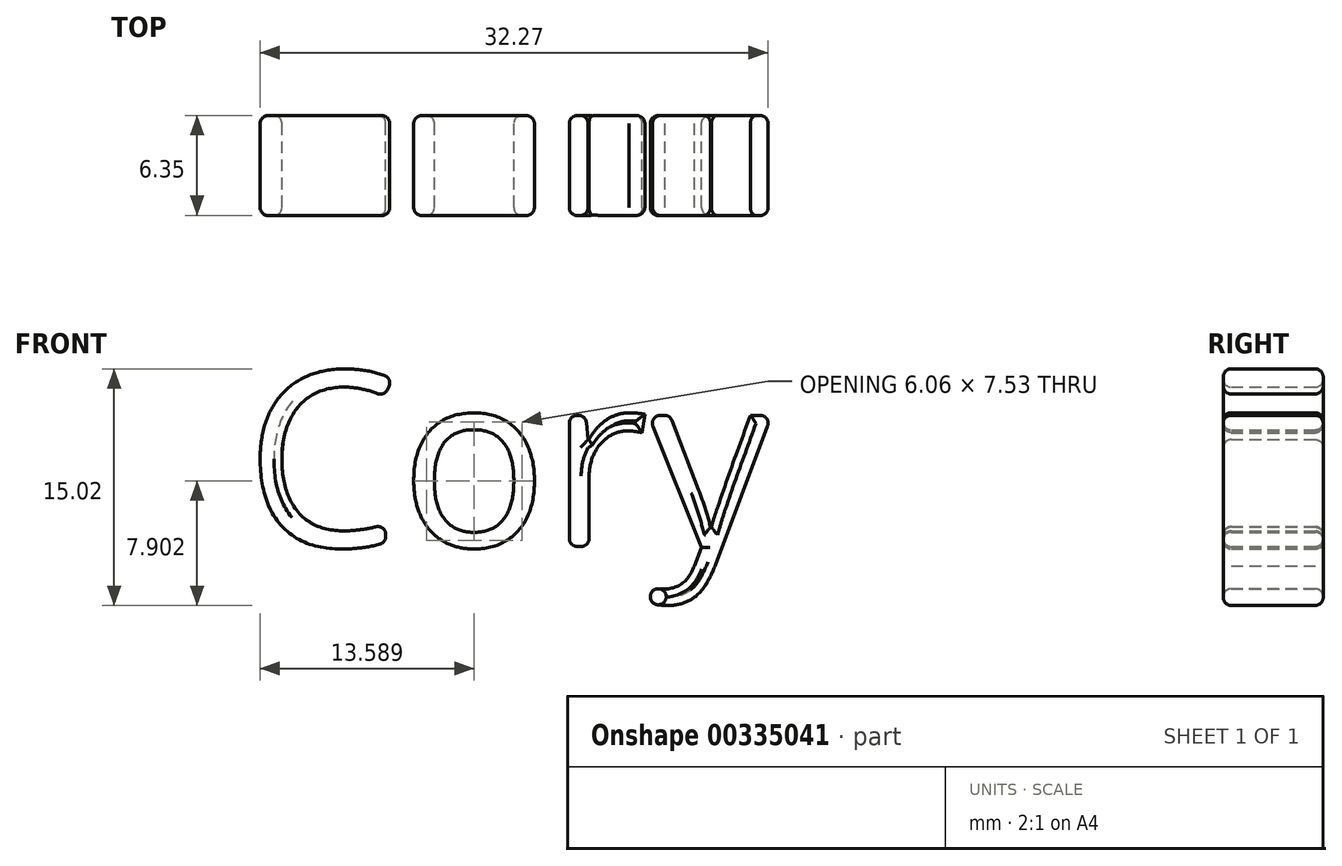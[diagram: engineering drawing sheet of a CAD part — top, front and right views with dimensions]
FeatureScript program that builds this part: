
annotation { "Feature Type Name" : "Feature", "Feature Type Description" : "" }
export const myFeature = defineFeature(function(context is Context, id is Id, definition is map)
    precondition{}
    {
        {
            var Q0;
            Q0=qCreatedBy(makeId("Front.planeOp"),FACE);
            var sketch = newSketch(context, id + "F0", { "sketchPlane" : qUnion([Q0])});
            skText(sketch, "E0", { "text": "Cory\n", "fontName": "OpenSans-Regular.ttf"});
            const initialGuessF0  = {"E0": [-0.05929, 0.0377, 1, 0, 0.01122]};
            skSetInitialGuess(sketch, initialGuessF0);
            skSolve(sketch);
        }
        {
            var Q0;
            Q0 = qSketchRegion(id + "F0", true);
            extrude(context, id + "F1", {"entities" : qUnion([Q0]), "depth" : 6.35 * mm});
        }
        {
            var Q0;
            Q0=makeQuery(id+"F1.opExtrude","SWEPT_FACE",FACE,{"disambiguationData":[OSD([sQuery(id+"F0.wireOp",EDGE,"E0.sketch_text.stroke-9")])]});
            var Q1;
            Q1=makeQuery(id+"F1.opExtrude","SWEPT_FACE",FACE,{"disambiguationData":[OSD([sQuery(id+"F0.wireOp",EDGE,"E0.sketch_text.stroke-8")])]});
            var Q2;
            Q2=makeQuery(id+"F1.opExtrude","CAP_EDGE",EDGE,{"disambiguationData":[OSD([sQuery(id+"F0.wireOp",EDGE,"E0.sketch_text.stroke-12")])],"isStart":false});
            var Q3;
            Q3=makeQuery(id+"F1.opExtrude","CAP_FACE",FACE,{"disambiguationData":[OSD([sQuery(id+"F0.wireOp",EDGE,"E0.sketch_text.stroke-0"),sQuery(id+"F0.wireOp",EDGE,"E0.sketch_text.stroke-1"),sQuery(id+"F0.wireOp",EDGE,"E0.sketch_text.stroke-2"),sQuery(id+"F0.wireOp",EDGE,"E0.sketch_text.stroke-3"),sQuery(id+"F0.wireOp",EDGE,"E0.sketch_text.stroke-4"),sQuery(id+"F0.wireOp",EDGE,"E0.sketch_text.stroke-5"),sQuery(id+"F0.wireOp",EDGE,"E0.sketch_text.stroke-6"),sQuery(id+"F0.wireOp",EDGE,"E0.sketch_text.stroke-7"),sQuery(id+"F0.wireOp",EDGE,"E0.sketch_text.stroke-8"),sQuery(id+"F0.wireOp",EDGE,"E0.sketch_text.stroke-9"),sQuery(id+"F0.wireOp",EDGE,"E0.sketch_text.stroke-10"),sQuery(id+"F0.wireOp",EDGE,"E0.sketch_text.stroke-11"),sQuery(id+"F0.wireOp",EDGE,"E0.sketch_text.stroke-12"),sQuery(id+"F0.wireOp",EDGE,"E0.sketch_text.stroke-13"),sQuery(id+"F0.wireOp",EDGE,"E0.sketch_text.stroke-14")])],"isStart":false});
            var Q4;
            Q4=makeQuery(id+"F1.opExtrude","SWEPT_FACE",FACE,{"disambiguationData":[OSD([sQuery(id+"F0.wireOp",EDGE,"E0.sketch_text.stroke-10")])]});
            var Q5;
            Q5=makeQuery(id+"F1.opExtrude","SWEPT_FACE",FACE,{"disambiguationData":[OSD([sQuery(id+"F0.wireOp",EDGE,"E0.sketch_text.stroke-11")])]});
            var Q6;
            Q6=makeQuery(id+"F1.opExtrude","SWEPT_FACE",FACE,{"disambiguationData":[OSD([sQuery(id+"F0.wireOp",EDGE,"E0.sketch_text.stroke-12")])]});
            var Q7;
            Q7=makeQuery(id+"F1.opExtrude","SWEPT_EDGE",EDGE,{"disambiguationData":[OSD([sQuery(id+"F0.wireOp",EDGE,"E0.sketch_text.stroke-4"),sQuery(id+"F0.wireOp",EDGE,"E0.sketch_text.stroke-5")])]});
            var Q8;
            Q8=makeQuery(id+"F1.opExtrude","SWEPT_FACE",FACE,{"disambiguationData":[OSD([sQuery(id+"F0.wireOp",EDGE,"E0.sketch_text.stroke-3")])]});
            var Q9;
            Q9=makeQuery(id+"F1.opExtrude","SWEPT_FACE",FACE,{"disambiguationData":[OSD([sQuery(id+"F0.wireOp",EDGE,"E0.sketch_text.stroke-2")])]});
            var Q10;
            Q10=makeQuery(id+"F1.opExtrude","SWEPT_FACE",FACE,{"disambiguationData":[OSD([sQuery(id+"F0.wireOp",EDGE,"E0.sketch_text.stroke-1")])]});
            var Q11;
            Q11=makeQuery(id+"F1.opExtrude","SWEPT_EDGE",EDGE,{"disambiguationData":[OSD([sQuery(id+"F0.wireOp",EDGE,"E0.sketch_text.stroke-5"),sQuery(id+"F0.wireOp",EDGE,"E0.sketch_text.stroke-6")])]});
            var Q12;
            Q12=makeQuery(id+"F1.opExtrude","SWEPT_FACE",FACE,{"disambiguationData":[OSD([sQuery(id+"F0.wireOp",EDGE,"E0.sketch_text.stroke-5")])]});
            var Q13;
            Q13=makeQuery(id+"F1.opExtrude","CAP_FACE",FACE,{"disambiguationData":[OSD([sQuery(id+"F0.wireOp",EDGE,"E0.sketch_text.stroke-15"),sQuery(id+"F0.wireOp",EDGE,"E0.sketch_text.stroke-16"),sQuery(id+"F0.wireOp",EDGE,"E0.sketch_text.stroke-17"),sQuery(id+"F0.wireOp",EDGE,"E0.sketch_text.stroke-18"),sQuery(id+"F0.wireOp",EDGE,"E0.sketch_text.stroke-19"),sQuery(id+"F0.wireOp",EDGE,"E0.sketch_text.stroke-20"),sQuery(id+"F0.wireOp",EDGE,"E0.sketch_text.stroke-21"),sQuery(id+"F0.wireOp",EDGE,"E0.sketch_text.stroke-22"),sQuery(id+"F0.wireOp",EDGE,"E0.sketch_text.stroke-23"),sQuery(id+"F0.wireOp",EDGE,"E0.sketch_text.stroke-24"),sQuery(id+"F0.wireOp",EDGE,"E0.sketch_text.stroke-25"),sQuery(id+"F0.wireOp",EDGE,"E0.sketch_text.stroke-26"),sQuery(id+"F0.wireOp",EDGE,"E0.sketch_text.stroke-27"),sQuery(id+"F0.wireOp",EDGE,"E0.sketch_text.stroke-28"),sQuery(id+"F0.wireOp",EDGE,"E0.sketch_text.stroke-29"),sQuery(id+"F0.wireOp",EDGE,"E0.sketch_text.stroke-30"),sQuery(id+"F0.wireOp",EDGE,"E0.sketch_text.stroke-31")])],"isStart":false});
            var Q14;
            Q14=makeQuery(id+"F1.opExtrude","CAP_FACE",FACE,{"disambiguationData":[OSD([sQuery(id+"F0.wireOp",EDGE,"E0.sketch_text.stroke-15"),sQuery(id+"F0.wireOp",EDGE,"E0.sketch_text.stroke-16"),sQuery(id+"F0.wireOp",EDGE,"E0.sketch_text.stroke-17"),sQuery(id+"F0.wireOp",EDGE,"E0.sketch_text.stroke-18"),sQuery(id+"F0.wireOp",EDGE,"E0.sketch_text.stroke-19"),sQuery(id+"F0.wireOp",EDGE,"E0.sketch_text.stroke-20"),sQuery(id+"F0.wireOp",EDGE,"E0.sketch_text.stroke-21"),sQuery(id+"F0.wireOp",EDGE,"E0.sketch_text.stroke-22"),sQuery(id+"F0.wireOp",EDGE,"E0.sketch_text.stroke-23"),sQuery(id+"F0.wireOp",EDGE,"E0.sketch_text.stroke-24"),sQuery(id+"F0.wireOp",EDGE,"E0.sketch_text.stroke-25"),sQuery(id+"F0.wireOp",EDGE,"E0.sketch_text.stroke-26"),sQuery(id+"F0.wireOp",EDGE,"E0.sketch_text.stroke-27"),sQuery(id+"F0.wireOp",EDGE,"E0.sketch_text.stroke-28"),sQuery(id+"F0.wireOp",EDGE,"E0.sketch_text.stroke-29"),sQuery(id+"F0.wireOp",EDGE,"E0.sketch_text.stroke-30"),sQuery(id+"F0.wireOp",EDGE,"E0.sketch_text.stroke-31")])],"isStart":true});
            var Q15;
            Q15=makeQuery(id+"F1.opExtrude","CAP_FACE",FACE,{"disambiguationData":[OSD([sQuery(id+"F0.wireOp",EDGE,"E0.sketch_text.stroke-32"),sQuery(id+"F0.wireOp",EDGE,"E0.sketch_text.stroke-33"),sQuery(id+"F0.wireOp",EDGE,"E0.sketch_text.stroke-34"),sQuery(id+"F0.wireOp",EDGE,"E0.sketch_text.stroke-35"),sQuery(id+"F0.wireOp",EDGE,"E0.sketch_text.stroke-36"),sQuery(id+"F0.wireOp",EDGE,"E0.sketch_text.stroke-37"),sQuery(id+"F0.wireOp",EDGE,"E0.sketch_text.stroke-38"),sQuery(id+"F0.wireOp",EDGE,"E0.sketch_text.stroke-39"),sQuery(id+"F0.wireOp",EDGE,"E0.sketch_text.stroke-40"),sQuery(id+"F0.wireOp",EDGE,"E0.sketch_text.stroke-41"),sQuery(id+"F0.wireOp",EDGE,"E0.sketch_text.stroke-42"),sQuery(id+"F0.wireOp",EDGE,"E0.sketch_text.stroke-43"),sQuery(id+"F0.wireOp",EDGE,"E0.sketch_text.stroke-44")])],"isStart":true});
            var Q16;
            Q16=makeQuery(id+"F1.opExtrude","SWEPT_FACE",FACE,{"disambiguationData":[OSD([sQuery(id+"F0.wireOp",EDGE,"E0.sketch_text.stroke-37")])]});
            var Q17;
            Q17=makeQuery(id+"F1.opExtrude","SWEPT_EDGE",EDGE,{"disambiguationData":[OSD([sQuery(id+"F0.wireOp",EDGE,"E0.sketch_text.stroke-38"),sQuery(id+"F0.wireOp",EDGE,"E0.sketch_text.stroke-39")])]});
            var Q18;
            Q18=makeQuery(id+"F1.opExtrude","SWEPT_FACE",FACE,{"disambiguationData":[OSD([sQuery(id+"F0.wireOp",EDGE,"E0.sketch_text.stroke-15")])]});
            var Q19;
            Q19=makeQuery(id+"F1.opExtrude","SWEPT_FACE",FACE,{"disambiguationData":[OSD([sQuery(id+"F0.wireOp",EDGE,"E0.sketch_text.stroke-52")])]});
            var Q20;
            Q20=makeQuery(id+"F1.opExtrude","CAP_FACE",FACE,{"disambiguationData":[OSD([sQuery(id+"F0.wireOp",EDGE,"E0.sketch_text.stroke-45"),sQuery(id+"F0.wireOp",EDGE,"E0.sketch_text.stroke-46"),sQuery(id+"F0.wireOp",EDGE,"E0.sketch_text.stroke-47"),sQuery(id+"F0.wireOp",EDGE,"E0.sketch_text.stroke-48"),sQuery(id+"F0.wireOp",EDGE,"E0.sketch_text.stroke-49"),sQuery(id+"F0.wireOp",EDGE,"E0.sketch_text.stroke-50"),sQuery(id+"F0.wireOp",EDGE,"E0.sketch_text.stroke-51"),sQuery(id+"F0.wireOp",EDGE,"E0.sketch_text.stroke-52"),sQuery(id+"F0.wireOp",EDGE,"E0.sketch_text.stroke-53"),sQuery(id+"F0.wireOp",EDGE,"E0.sketch_text.stroke-54"),sQuery(id+"F0.wireOp",EDGE,"E0.sketch_text.stroke-55"),sQuery(id+"F0.wireOp",EDGE,"E0.sketch_text.stroke-56"),sQuery(id+"F0.wireOp",EDGE,"E0.sketch_text.stroke-57"),sQuery(id+"F0.wireOp",EDGE,"E0.sketch_text.stroke-58"),sQuery(id+"F0.wireOp",EDGE,"E0.sketch_text.stroke-59"),sQuery(id+"F0.wireOp",EDGE,"E0.sketch_text.stroke-60")])],"isStart":false});
            var Q21;
            Q21=makeQuery(id+"F1.opExtrude","CAP_FACE",FACE,{"disambiguationData":[OSD([sQuery(id+"F0.wireOp",EDGE,"E0.sketch_text.stroke-32"),sQuery(id+"F0.wireOp",EDGE,"E0.sketch_text.stroke-33"),sQuery(id+"F0.wireOp",EDGE,"E0.sketch_text.stroke-34"),sQuery(id+"F0.wireOp",EDGE,"E0.sketch_text.stroke-35"),sQuery(id+"F0.wireOp",EDGE,"E0.sketch_text.stroke-36"),sQuery(id+"F0.wireOp",EDGE,"E0.sketch_text.stroke-37"),sQuery(id+"F0.wireOp",EDGE,"E0.sketch_text.stroke-38"),sQuery(id+"F0.wireOp",EDGE,"E0.sketch_text.stroke-39"),sQuery(id+"F0.wireOp",EDGE,"E0.sketch_text.stroke-40"),sQuery(id+"F0.wireOp",EDGE,"E0.sketch_text.stroke-41"),sQuery(id+"F0.wireOp",EDGE,"E0.sketch_text.stroke-42"),sQuery(id+"F0.wireOp",EDGE,"E0.sketch_text.stroke-43"),sQuery(id+"F0.wireOp",EDGE,"E0.sketch_text.stroke-44")])],"isStart":false});
            var Q22;
            Q22=makeQuery(id+"F1.opExtrude","SWEPT_FACE",FACE,{"disambiguationData":[OSD([sQuery(id+"F0.wireOp",EDGE,"E0.sketch_text.stroke-39")])]});
            var Q23;
            Q23=makeQuery(id+"F1.opExtrude","SWEPT_FACE",FACE,{"disambiguationData":[OSD([sQuery(id+"F0.wireOp",EDGE,"E0.sketch_text.stroke-40")])]});
            var Q24;
            Q24=makeQuery(id+"F1.opExtrude","SWEPT_FACE",FACE,{"disambiguationData":[OSD([sQuery(id+"F0.wireOp",EDGE,"E0.sketch_text.stroke-45")])]});
            var Q25;
            Q25=makeQuery(id+"F1.opExtrude","SWEPT_FACE",FACE,{"disambiguationData":[OSD([sQuery(id+"F0.wireOp",EDGE,"E0.sketch_text.stroke-46")])]});
            var Q26;
            Q26=makeQuery(id+"F1.opExtrude","CAP_FACE",FACE,{"disambiguationData":[OSD([sQuery(id+"F0.wireOp",EDGE,"E0.sketch_text.stroke-45"),sQuery(id+"F0.wireOp",EDGE,"E0.sketch_text.stroke-46"),sQuery(id+"F0.wireOp",EDGE,"E0.sketch_text.stroke-47"),sQuery(id+"F0.wireOp",EDGE,"E0.sketch_text.stroke-48"),sQuery(id+"F0.wireOp",EDGE,"E0.sketch_text.stroke-49"),sQuery(id+"F0.wireOp",EDGE,"E0.sketch_text.stroke-50"),sQuery(id+"F0.wireOp",EDGE,"E0.sketch_text.stroke-51"),sQuery(id+"F0.wireOp",EDGE,"E0.sketch_text.stroke-52"),sQuery(id+"F0.wireOp",EDGE,"E0.sketch_text.stroke-53"),sQuery(id+"F0.wireOp",EDGE,"E0.sketch_text.stroke-54"),sQuery(id+"F0.wireOp",EDGE,"E0.sketch_text.stroke-55"),sQuery(id+"F0.wireOp",EDGE,"E0.sketch_text.stroke-56"),sQuery(id+"F0.wireOp",EDGE,"E0.sketch_text.stroke-57"),sQuery(id+"F0.wireOp",EDGE,"E0.sketch_text.stroke-58"),sQuery(id+"F0.wireOp",EDGE,"E0.sketch_text.stroke-59"),sQuery(id+"F0.wireOp",EDGE,"E0.sketch_text.stroke-60")])],"isStart":true});
            var Q27;
            Q27=makeQuery(id+"F1.opExtrude","SWEPT_FACE",FACE,{"disambiguationData":[OSD([sQuery(id+"F0.wireOp",EDGE,"E0.sketch_text.stroke-13")])]});
            var Q28;
            Q28=makeQuery(id+"F1.opExtrude","SWEPT_FACE",FACE,{"disambiguationData":[OSD([sQuery(id+"F0.wireOp",EDGE,"E0.sketch_text.stroke-56")])]});
            fillet(context, id + "F2", {"entities" : qUnion([Q0, Q1, Q2, Q3, Q4, Q5, Q6, Q7, Q8, Q9, Q10, Q11, Q12, Q13, Q14, Q15, Q16, Q17, Q18, Q19, Q20, Q21, Q22, Q23, Q24, Q25, Q26, Q27, Q28]), "radius" : 0.5 * mm, "tangentPropagation" : true, "allowEdgeOverflow" : false});
        }
    });
